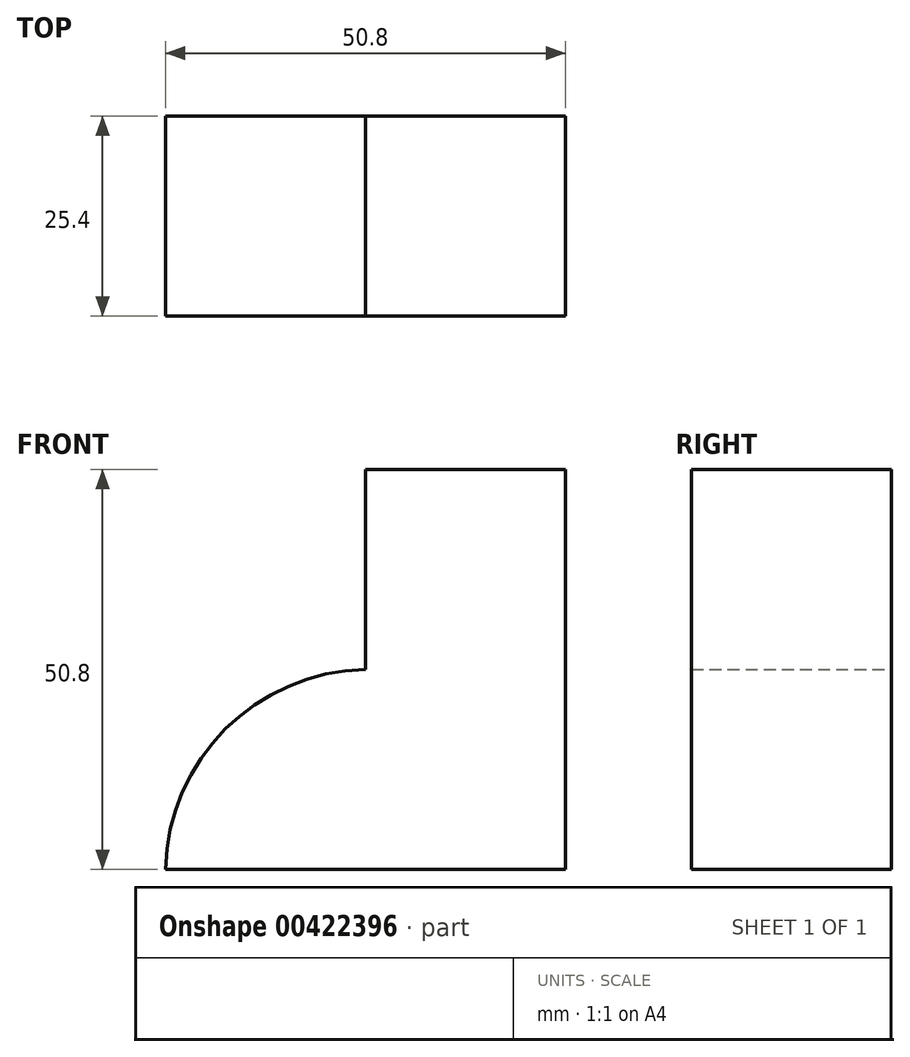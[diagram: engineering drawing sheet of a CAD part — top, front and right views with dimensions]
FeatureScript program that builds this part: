
annotation { "Feature Type Name" : "Feature", "Feature Type Description" : "" }
export const myFeature = defineFeature(function(context is Context, id is Id, definition is map)
    precondition{}
    {
        {
            var Q0;
            Q0=qCreatedBy(makeId("Front.planeOp"),FACE);
            var sketch = newSketch(context, id + "F0", { "sketchPlane" : qUnion([Q0])});
            skLineSegment(sketch, "E0", {"start": v(0, 0) * mm, "end": v(50.8, 0) * mm});
            skLineSegment(sketch, "E1", {"start": v(50.8, 0) * mm, "end": v(50.8, 50.8) * mm});
            skLineSegment(sketch, "E2", {"start": v(50.8, 50.8) * mm, "end": v(25.4, 50.8) * mm});
            skLineSegment(sketch, "E3", {"start": v(25.4, 50.8) * mm, "end": v(25.4, 25.4) * mm});
            skArc(sketch, "E4", {"start": v(25.4, 25.4) * mm, "mid": v(7.58, 17.82) * mm, "end": v(0, 0) * mm});
            skSolve(sketch);
        }
        {
            var Q0;
            Q0 = qSketchRegion(id + "F0", true);
            extrude(context, id + "F1", {"entities" : qUnion([Q0]), "depth" : 25.4 * mm});
        }
    });
